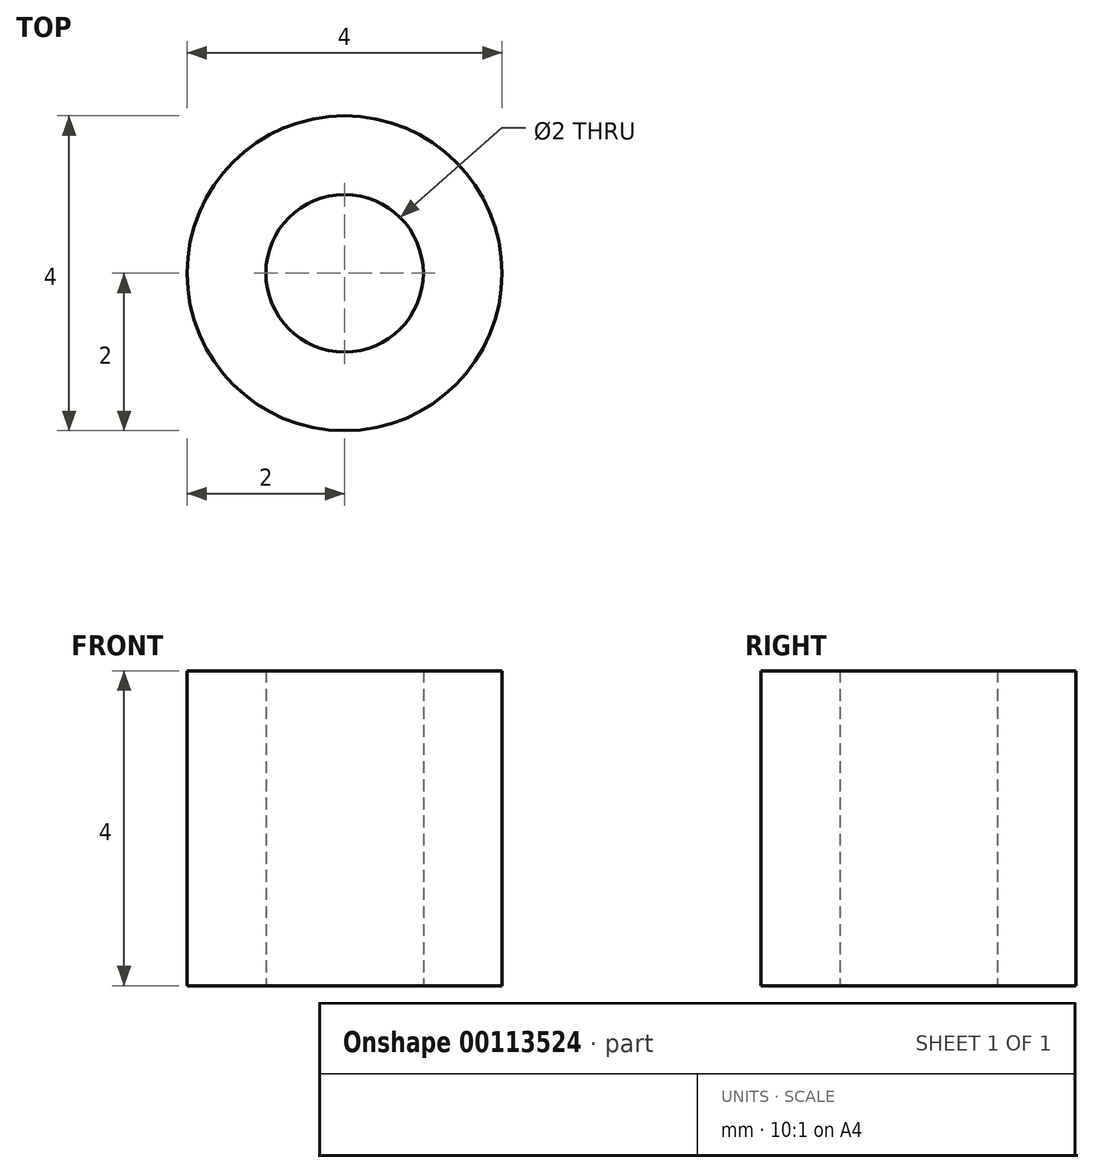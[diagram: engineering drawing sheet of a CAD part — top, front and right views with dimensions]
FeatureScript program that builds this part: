
annotation { "Feature Type Name" : "Feature", "Feature Type Description" : "" }
export const myFeature = defineFeature(function(context is Context, id is Id, definition is map)
    precondition{}
    {
        {
            var Q0;
            Q0=qCreatedBy(makeId("Top.planeOp"),FACE);
            var sketch = newSketch(context, id + "F0", { "sketchPlane" : qUnion([Q0])});
            skCircle(sketch, "E0", {"center": v(0, 0) * mm, "radius": 1 * mm});
            skCircle(sketch, "E1", {"center": v(0, 0) * mm, "radius": 2 * mm});
            skSolve(sketch);
        }
        {
            var Q0;
            Q0 = qSketchRegion(id + "F0", true);
            extrude(context, id + "F1", {"entities" : qUnion([Q0]), "depth" : 4 * mm});
        }
    });
